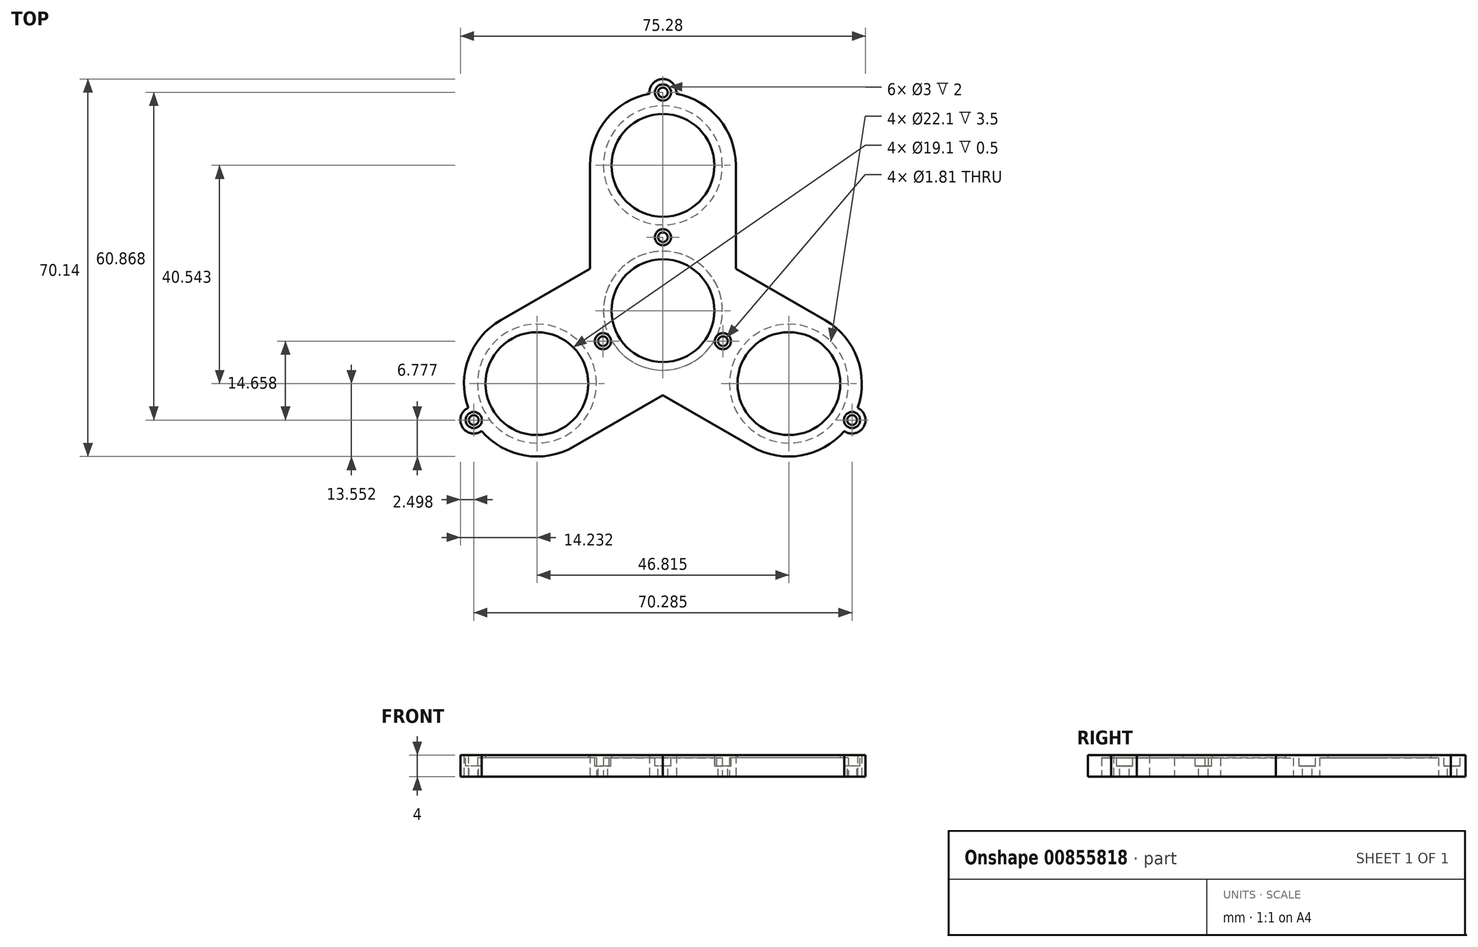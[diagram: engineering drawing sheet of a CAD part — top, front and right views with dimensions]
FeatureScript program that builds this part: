
annotation { "Feature Type Name" : "Feature", "Feature Type Description" : "" }
export const myFeature = defineFeature(function(context is Context, id is Id, definition is map)
    precondition{}
    {
        {
            var Q0;
            Q0=qCreatedBy(makeId("Top.planeOp"),FACE);
            var sketch = newSketch(context, id + "F0", { "sketchPlane" : qUnion([Q0])});
            skCircle(sketch, "E0", {"center": v(0, -0.78) * mm, "radius": 11.05 * mm});
            skCircle(sketch, "E1", {"center": v(0, 26.22) * mm, "radius": 11.05 * mm});
            skLineSegment(sketch, "E2", {"start": v(-13.55, 26.22) * mm, "end": v(-13.55, 7.02) * mm});
            skLineSegment(sketch, "E3", {"start": v(13.55, 26.22) * mm, "end": v(13.55, 7.02) * mm});
            skArc(sketch, "E4", {"start": v(-13.55, 26.22) * mm, "mid": v(0, 12.67) * mm, "end": v(13.55, 26.22) * mm, "construction": true});
            skArc(sketch, "E5", {"start": v(13.55, 26.22) * mm, "mid": v(0, 39.77) * mm, "end": v(-13.55, 26.22) * mm});
            skArc(sketch, "E6", {"start": v(-13.55, -0.78) * mm, "mid": v(0, -14.33) * mm, "end": v(13.55, -0.78) * mm, "construction": true});
            skArc(sketch, "E7", {"start": v(13.55, -0.78) * mm, "mid": v(0, 12.77) * mm, "end": v(-13.55, -0.78) * mm, "construction": true});
            skArc(sketch, "E8.1.0", {"start": v(-30.18, -2.58) * mm, "mid": v(-35.14, -21.1) * mm, "end": v(-16.63, -26.05) * mm});
            skCircle(sketch, "E8.1.1", {"center": v(-23.4, -14.32) * mm, "radius": 11.05 * mm});
            skLineSegment(sketch, "E8.1.2", {"start": v(-16.63, -26.05) * mm, "end": v(0, -16.45) * mm});
            skLineSegment(sketch, "E8.1.3", {"start": v(-30.18, -2.58) * mm, "end": v(-13.55, 7.02) * mm});
            skArc(sketch, "E8.2.0", {"start": v(16.63, -26.05) * mm, "mid": v(35.14, -21.1) * mm, "end": v(30.18, -2.58) * mm});
            skCircle(sketch, "E8.2.1", {"center": v(23.4, -14.32) * mm, "radius": 11.05 * mm});
            skLineSegment(sketch, "E8.2.2", {"start": v(30.18, -2.58) * mm, "end": v(13.55, 7.02) * mm});
            skLineSegment(sketch, "E8.2.3", {"start": v(16.63, -26.05) * mm, "end": v(0, -16.45) * mm});
            skPoint(sketch, "E8.center", {"position": v(0, -0.8) * mm});
            skLineSegment(sketch, "E9", {"start": v(-13.55, 7.02) * mm, "end": v(-13.55, -0.78) * mm, "construction": true});
            skLineSegment(sketch, "E10", {"start": v(-13.55, 7.02) * mm, "end": v(-6.8, 10.92) * mm, "construction": true});
            skLineSegment(sketch, "E11", {"start": v(0, -16.45) * mm, "end": v(-6.75, -12.55) * mm, "construction": true});
            skLineSegment(sketch, "E12", {"start": v(0, -16.45) * mm, "end": v(6.75, -12.55) * mm, "construction": true});
            skLineSegment(sketch, "E13", {"start": v(13.55, 7.02) * mm, "end": v(6.8, 10.92) * mm, "construction": true});
            skLineSegment(sketch, "E14", {"start": v(13.55, 7.02) * mm, "end": v(13.55, -0.78) * mm, "construction": true});
            skArc(sketch, "E15", {"start": v(-2.49, 39.54) * mm, "mid": v(0, 37.27) * mm, "end": v(2.49, 39.54) * mm, "construction": true});
            skArc(sketch, "E16", {"start": v(2.49, 39.54) * mm, "mid": v(0, 42.27) * mm, "end": v(-2.49, 39.54) * mm});
            skArc(sketch, "E17", {"start": v(-36.19, -18.82) * mm, "mid": v(-37.3, -22.34) * mm, "end": v(-33.7, -23.13) * mm});
            skArc(sketch, "E18", {"start": v(-33.7, -23.13) * mm, "mid": v(-32.98, -19.84) * mm, "end": v(-36.19, -18.82) * mm, "construction": true});
            skArc(sketch, "E19", {"start": v(33.7, -23.13) * mm, "mid": v(37.3, -22.34) * mm, "end": v(36.19, -18.82) * mm});
            skArc(sketch, "E20", {"start": v(36.19, -18.82) * mm, "mid": v(32.98, -19.84) * mm, "end": v(33.7, -23.13) * mm, "construction": true});
            skSolve(sketch);
        }
        {
            var Q0;
            Q0=makeQuery(id+"F0.imprint","IMPRINT",FACE,{"disambiguationData":[TD([[makeQuery(id+"F0.imprint","IMPRINT",EDGE,{"derivedFrom":sQuery(id+"F0.wireOp",EDGE,"E0")}),-1.0]])]});
            var Q1;
            {var subQ0=sQuery(id+"F0.wireOp",EDGE,"E16");Q1=makeQuery(id+"F0.imprint","IMPRINT",FACE,{"disambiguationData":[TD([[makeQuery(id+"F0.imprint","IMPRINT",EDGE,{"derivedFrom":subQ0}),1.0]])]});}
            var Q2;
            {var subQ0=sQuery(id+"F0.wireOp",EDGE,"E17");Q2=makeQuery(id+"F0.imprint","IMPRINT",FACE,{"disambiguationData":[TD([[makeQuery(id+"F0.imprint","IMPRINT",EDGE,{"derivedFrom":subQ0}),1.0]])]});}
            var Q3;
            {var subQ0=sQuery(id+"F0.wireOp",EDGE,"E19");Q3=makeQuery(id+"F0.imprint","IMPRINT",FACE,{"disambiguationData":[TD([[makeQuery(id+"F0.imprint","IMPRINT",EDGE,{"derivedFrom":subQ0}),1.0]])]});}
            extrude(context, id + "F1", {"entities" : qUnion([Q0, Q1, Q2, Q3]), "depth" : 3.5 * mm, "offsetDistance" : 25 * mm});
        }
        {
            var Q0;
            Q0=makeQuery(id+"F1.opExtrude","CAP_FACE",FACE,{"disambiguationData":[OSD([sQuery(id+"F0.wireOp",EDGE,"E0"),sQuery(id+"F0.wireOp",EDGE,"E1"),sQuery(id+"F0.wireOp",EDGE,"E2"),sQuery(id+"F0.wireOp",EDGE,"E3"),sQuery(id+"F0.wireOp",EDGE,"E5"),sQuery(id+"F0.wireOp",EDGE,"E8.1.0"),sQuery(id+"F0.wireOp",EDGE,"E8.1.1"),sQuery(id+"F0.wireOp",EDGE,"E8.1.2"),sQuery(id+"F0.wireOp",EDGE,"E8.1.3"),sQuery(id+"F0.wireOp",EDGE,"E8.2.0"),sQuery(id+"F0.wireOp",EDGE,"E8.2.1"),sQuery(id+"F0.wireOp",EDGE,"E8.2.2"),sQuery(id+"F0.wireOp",EDGE,"E8.2.3")])],"isStart":false});
            var sketch = newSketch(context, id + "F2", { "sketchPlane" : qUnion([Q0])});
            skCircle(sketch, "E21", {"center": v(0, -0.78) * mm, "radius": 9.55 * mm});
            skCircle(sketch, "E22", {"center": v(-23.4, -14.32) * mm, "radius": 9.55 * mm});
            skCircle(sketch, "E23", {"center": v(23.4, -14.32) * mm, "radius": 9.55 * mm});
            skCircle(sketch, "E24", {"center": v(0, 26.22) * mm, "radius": 9.55 * mm});
            skSolve(sketch);
        }
        {
            var Q0;
            Q0=makeQuery(id+"F2.imprint","IMPRINT",FACE,{"disambiguationData":[TD([[makeQuery(id+"F2.imprint","IMPRINT",EDGE,{"derivedFrom":sQuery(id+"F2.wireOp",EDGE,"E24")}),-1.0]])]});
            var Q1;
            Q1=makeQuery(id+"F2.imprint","IMPRINT",FACE,{"disambiguationData":[TD([[makeQuery(id+"F2.imprint","IMPRINT",EDGE,{"derivedFrom":sQuery(id+"F2.wireOp",EDGE,"E21")}),-1.0]])]});
            var Q2;
            Q2=makeQuery(id+"F2.imprint","IMPRINT",FACE,{"disambiguationData":[TD([[makeQuery(id+"F2.imprint","IMPRINT",EDGE,{"derivedFrom":sQuery(id+"F2.wireOp",EDGE,"E22")}),-1.0]])]});
            var Q3;
            Q3=makeQuery(id+"F2.imprint","IMPRINT",FACE,{"disambiguationData":[TD([[makeQuery(id+"F2.imprint","IMPRINT",EDGE,{"derivedFrom":sQuery(id+"F2.wireOp",EDGE,"E23")}),-1.0]])]});
            var Q4;
            Q4=makeQuery(id+"F2.imprint","IMPRINT",FACE,{"disambiguationData":[TD([[makeQuery(id+"F2.imprint","IMPRINT",EDGE,{"derivedFrom":makeQuery(id+"F1.opExtrude","CAP_EDGE",EDGE,{"disambiguationData":[OSD([sQuery(id+"F0.wireOp",EDGE,"E0")])],"isStart":false})}),-1.0]])]});
            extrude(context, id + "F3", {"entities" : qUnion([Q0, Q1, Q2, Q3, Q4]), "operationType" : NewBodyOperationType.ADD, "depth" : .5 * mm, "offsetDistance" : 25 * mm});
        }
        {
            var Q0;
            Q0=makeQuery(id+"F3.opExtrude","CAP_FACE",FACE,{"disambiguationData":[OSD([sQuery(id+"F0.wireOp",EDGE,"E2"),sQuery(id+"F0.wireOp",EDGE,"E3"),sQuery(id+"F0.wireOp",EDGE,"E5"),sQuery(id+"F0.wireOp",EDGE,"E8.1.0"),sQuery(id+"F0.wireOp",EDGE,"E8.1.2"),sQuery(id+"F0.wireOp",EDGE,"E8.1.3"),sQuery(id+"F0.wireOp",EDGE,"E8.2.0"),sQuery(id+"F0.wireOp",EDGE,"E8.2.2"),sQuery(id+"F0.wireOp",EDGE,"E8.2.3"),sQuery(id+"F0.wireOp",EDGE,"E16"),sQuery(id+"F0.wireOp",EDGE,"E17"),sQuery(id+"F0.wireOp",EDGE,"E19"),sQuery(id+"F2.wireOp",EDGE,"E21"),sQuery(id+"F2.wireOp",EDGE,"E22"),sQuery(id+"F2.wireOp",EDGE,"E23"),sQuery(id+"F2.wireOp",EDGE,"E24")])],"isStart":false});
            var sketch = newSketch(context, id + "F4", { "sketchPlane" : qUnion([Q0])});
            skCircle(sketch, "E25", {"center": v(0, 39.77) * mm, "radius": 1.5 * mm});
            skCircle(sketch, "E26", {"center": v(-35.14, -21.1) * mm, "radius": 1.5 * mm});
            skCircle(sketch, "E27", {"center": v(35.14, -21.1) * mm, "radius": 1.5 * mm});
            skCircle(sketch, "E28", {"center": v(0, 12.87) * mm, "radius": 1.5 * mm});
            skCircle(sketch, "E29.1.0", {"center": v(-11.15, -6.44) * mm, "radius": 1.5 * mm});
            skCircle(sketch, "E29.2.0", {"center": v(11.15, -6.44) * mm, "radius": 1.5 * mm});
            skPoint(sketch, "E29.center", {"position": v(0, 0) * mm});
            skSolve(sketch);
        }
        {
            var Q0;
            Q0 = qSketchRegion(id + "F4", true);
            extrude(context, id + "F5", {"entities" : qUnion([Q0]), "operationType" : NewBodyOperationType.REMOVE, "oppositeDirection" : true, "depth" : 2 * mm, "offsetDistance" : 25 * mm});
        }
        {
            var Q0;
            Q0=makeQuery(id+"F5.boolean.opBoolean","COPY",FACE,{"derivedFrom":makeQuery(id+"F5.opExtrude","CAP_FACE",FACE,{"disambiguationData":[OSD([sQuery(id+"F4.wireOp",EDGE,"E25")])],"isStart":false})});
            var sketch = newSketch(context, id + "F6", { "sketchPlane" : qUnion([Q0])});
            skCircle(sketch, "E30", {"center": v(0, 39.77) * mm, "radius": 0.9 * mm});
            skCircle(sketch, "E31", {"center": v(0, 12.87) * mm, "radius": 0.9 * mm});
            skCircle(sketch, "E32", {"center": v(-11.15, -6.44) * mm, "radius": 0.9 * mm});
            skCircle(sketch, "E33", {"center": v(-35.14, -21.1) * mm, "radius": 0.9 * mm});
            skCircle(sketch, "E34", {"center": v(11.15, -6.44) * mm, "radius": 0.9 * mm});
            skCircle(sketch, "E35", {"center": v(35.14, -21.1) * mm, "radius": 0.9 * mm});
            skSolve(sketch);
        }
        {
            var Q0;
            Q0 = qSketchRegion(id + "F6", true);
            extrude(context, id + "F7", {"entities" : qUnion([Q0]), "operationType" : NewBodyOperationType.REMOVE, "endBound" : BoundingType.UP_TO_NEXT, "oppositeDirection" : true, "depth" : 25 * mm, "offsetDistance" : 25 * mm});
        }
    });
